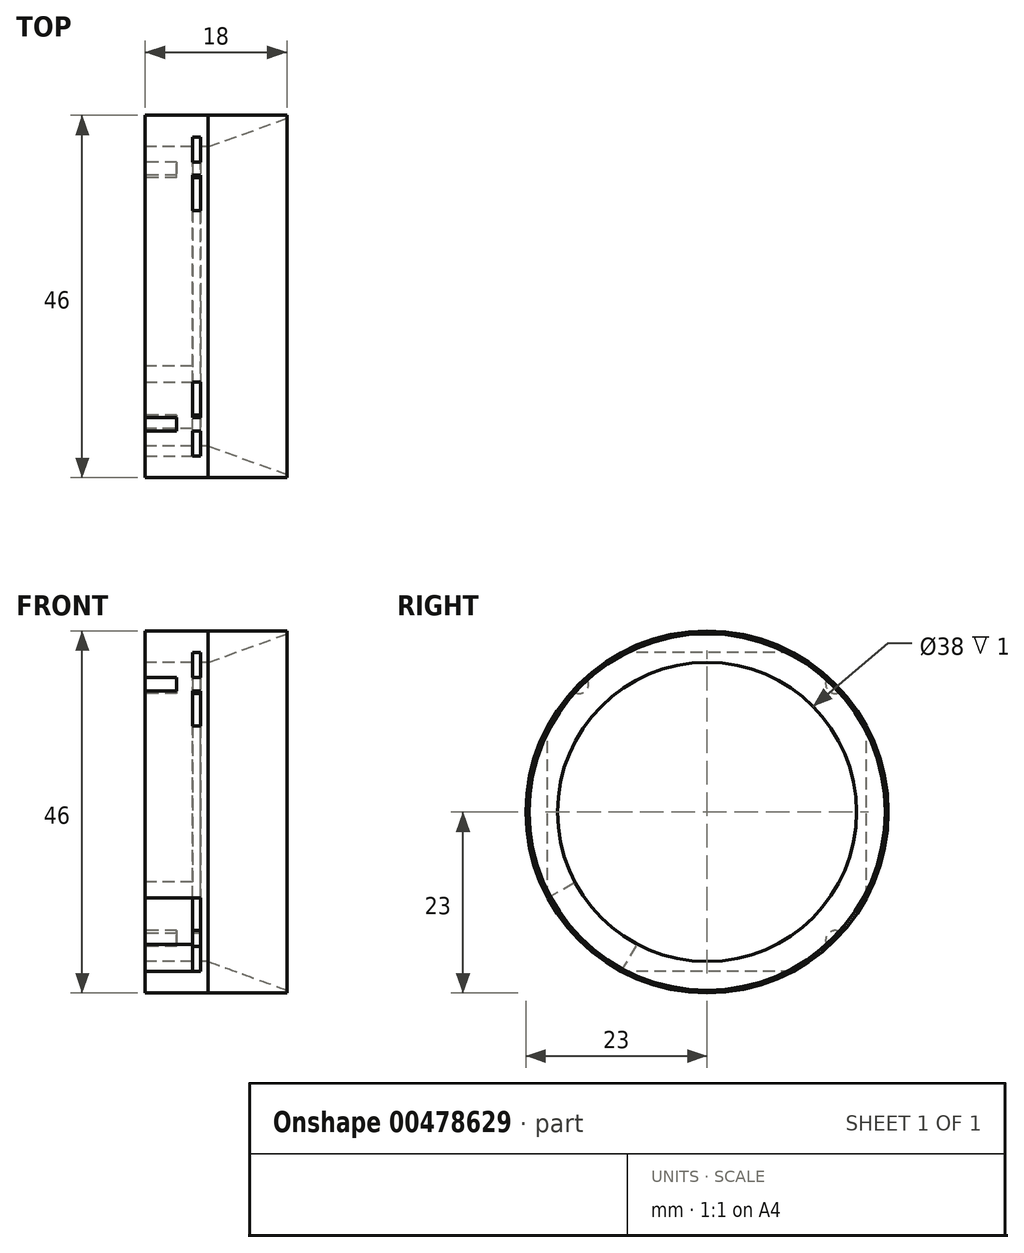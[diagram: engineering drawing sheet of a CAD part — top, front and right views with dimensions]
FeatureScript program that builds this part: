
annotation { "Feature Type Name" : "Feature", "Feature Type Description" : "" }
export const myFeature = defineFeature(function(context is Context, id is Id, definition is map)
    precondition{}
    {
        {
            var Q0;
            Q0=qCreatedBy(makeId("Right.planeOp"),FACE);
            var sketch = newSketch(context, id + "F0", { "sketchPlane" : qUnion([Q0])});
            skLineSegment(sketch, "E0.bottom", {"start": v(10.9, -20.25) * mm, "end": v(-10.9, -20.25) * mm});
            skLineSegment(sketch, "E0.top", {"start": v(10.9, 20.25) * mm, "end": v(-10.9, 20.25) * mm});
            skLineSegment(sketch, "E0.left", {"start": v(20.25, -10.9) * mm, "end": v(20.25, 10.9) * mm});
            skLineSegment(sketch, "E0.right", {"start": v(-20.25, -10.9) * mm, "end": v(-20.25, 10.9) * mm});
            skPoint(sketch, "E0.middle", {"position": v(0, 0) * mm});
            skPoint(sketch, "E1.visualSharp", {"position": v(-20.25, 20.25) * mm});
            skPoint(sketch, "E2.visualSharp", {"position": v(20.25, 20.25) * mm});
            skPoint(sketch, "E3.visualSharp", {"position": v(20.25, -20.25) * mm});
            skPoint(sketch, "E4.visualSharp", {"position": v(-20.25, -20.25) * mm});
            skCircle(sketch, "E5", {"center": v(0, 0) * mm, "radius": 23 * mm});
            skLineSegment(sketch, "E6", {"start": v(0, 0) * mm, "end": v(18.25, 18.25) * mm, "construction": true});
            skArc(sketch, "E7", {"start": v(15.4, 17.09) * mm, "mid": v(15.41, 15.41) * mm, "end": v(17.09, 15.4) * mm});
            skArc(sketch, "E8.MirrorC", {"start": v(15.4, -17.09) * mm, "mid": v(15.41, -15.41) * mm, "end": v(17.09, -15.4) * mm});
            skArc(sketch, "E9.MirrorC", {"start": v(-15.4, 17.09) * mm, "mid": v(-15.41, 15.41) * mm, "end": v(-17.09, 15.4) * mm});
            skArc(sketch, "E10.MirrorC", {"start": v(-15.4, -17.09) * mm, "mid": v(-15.41, -15.41) * mm, "end": v(-17.09, -15.4) * mm});
            skCircle(sketch, "E11", {"center": v(0, 0) * mm, "radius": 19 * mm});
            skLineSegment(sketch, "E12", {"start": v(-10.9, -20.25) * mm, "end": v(-8.83, -16.82) * mm});
            skLineSegment(sketch, "E13", {"start": v(-20.25, -10.9) * mm, "end": v(-16.8, -8.9) * mm});
            skSolve(sketch);
        }
        {
            var Q0;
            Q0 = qSketchRegion(id + "F0", true);
            extrude(context, id + "F1", {"entities" : qUnion([Q0]), "depth" : 4 * mm});
        }
        {
            var Q0;
            {var subQ3=sQuery(id+"F0.wireOp",EDGE,"E0.bottom");Q0=makeQuery(id+"F0.imprint","IMPRINT",FACE,{"disambiguationData":[TD([[makeQuery(id+"F0.imprint","IMPRINT",EDGE,{"derivedFrom":subQ3}),-1.0]])]});}
            var Q1;
            {var subQ0=sQuery(id+"F0.wireOp",EDGE,"E10.MirrorC");Q1=makeQuery(id+"F0.imprint","IMPRINT",FACE,{"disambiguationData":[TD([[makeQuery(id+"F0.imprint","IMPRINT",EDGE,{"derivedFrom":subQ0}),-1.0]])]});}
            var Q2;
            {var subQ0=sQuery(id+"F0.wireOp",EDGE,"E10.MirrorC");Q2=makeQuery(id+"F0.imprint","IMPRINT",FACE,{"disambiguationData":[TD([[makeQuery(id+"F0.imprint","IMPRINT",EDGE,{"derivedFrom":subQ0}),1.0]])]});}
            extrude(context, id + "F2", {"entities" : qUnion([Q0, Q1, Q2]), "operationType" : NewBodyOperationType.REMOVE, "depth" : 3 * mm});
        }
        {
            var Q0;
            {var subQ6=sQuery(id+"F0.wireOp",EDGE,"E0.bottom");Q0=makeQuery(id+"F0.imprint","IMPRINT",FACE,{"disambiguationData":[TD([[makeQuery(id+"F0.imprint","IMPRINT",EDGE,{"derivedFrom":subQ6}),-1.0]])]});}
            extrude(context, id + "F3", {"entities" : qUnion([Q0]), "depth" : 2 * mm});
        }
        {
            var Q0;
            {var subQ0=sQuery(id+"F0.wireOp",EDGE,"E0.bottom");Q0=makeQuery(id+"F0.imprint","IMPRINT",FACE,{"disambiguationData":[TD([[makeQuery(id+"F0.imprint","IMPRINT",EDGE,{"derivedFrom":subQ0}),1.0]])]});}
            var Q1;
            {var subQ0=sQuery(id+"F0.wireOp",EDGE,"E0.top");Q1=makeQuery(id+"F0.imprint","IMPRINT",FACE,{"disambiguationData":[TD([[makeQuery(id+"F0.imprint","IMPRINT",EDGE,{"derivedFrom":subQ0}),-1.0]])]});}
            var Q2;
            {var subQ0=sQuery(id+"F0.wireOp",EDGE,"E0.left");Q2=makeQuery(id+"F0.imprint","IMPRINT",FACE,{"disambiguationData":[TD([[makeQuery(id+"F0.imprint","IMPRINT",EDGE,{"derivedFrom":subQ0}),-1.0]])]});}
            var Q3;
            {var subQ0=sQuery(id+"F0.wireOp",EDGE,"E0.right");Q3=makeQuery(id+"F0.imprint","IMPRINT",FACE,{"disambiguationData":[TD([[makeQuery(id+"F0.imprint","IMPRINT",EDGE,{"derivedFrom":subQ0}),1.0]])]});}
            var Q4;
            {var subQ0=sQuery(id+"F0.wireOp",EDGE,"E7");Q4=makeQuery(id+"F0.imprint","IMPRINT",FACE,{"disambiguationData":[TD([[makeQuery(id+"F0.imprint","IMPRINT",EDGE,{"derivedFrom":subQ0}),1.0]])]});}
            var Q5;
            {var subQ0=sQuery(id+"F0.wireOp",EDGE,"E9.MirrorC");Q5=makeQuery(id+"F0.imprint","IMPRINT",FACE,{"disambiguationData":[TD([[makeQuery(id+"F0.imprint","IMPRINT",EDGE,{"derivedFrom":subQ0}),-1.0]])]});}
            var Q6;
            {var subQ0=sQuery(id+"F0.wireOp",EDGE,"E8.MirrorC");Q6=makeQuery(id+"F0.imprint","IMPRINT",FACE,{"disambiguationData":[TD([[makeQuery(id+"F0.imprint","IMPRINT",EDGE,{"derivedFrom":subQ0}),-1.0]])]});}
            var Q7;
            {var subQ3=sQuery(id+"F0.wireOp",EDGE,"E0.bottom");Q7=makeQuery(id+"F0.imprint","IMPRINT",FACE,{"disambiguationData":[TD([[makeQuery(id+"F0.imprint","IMPRINT",EDGE,{"derivedFrom":subQ3}),-1.0]])]});}
            extrude(context, id + "F4", {"entities" : qUnion([Q0, Q1, Q2, Q3, Q4, Q5, Q6, Q7]), "operationType" : NewBodyOperationType.ADD, "oppositeDirection" : true, "depth" : 4 * mm});
        }
        {
            var Q0;
            Q0=makeQuery(id+"F1.opExtrude","CAP_FACE",FACE,{"disambiguationData":[OSD([sQuery(id+"F0.wireOp",EDGE,"E5"),sQuery(id+"F0.wireOp",EDGE,"E11")])],"isStart":false});
            extrude(context, id + "F5", {"entities" : qUnion([Q0]), "depth" : 10 * mm});
        }
        {
            var Q0;
            Q0=makeQuery(id+"F5.opExtrude","CAP_EDGE",EDGE,{"disambiguationData":[OSD([sQuery(id+"F0.wireOp",EDGE,"E11")])],"isStart":false});
            chamfer(context, id + "F6", {"entities" : qUnion([Q0]), "chamferType" : ChamferType.OFFSET_ANGLE, "width" : 10 * mm, "oppositeDirection" : false, "angle" : 20 * degree, "tangentPropagation" : true});
        }
    });
